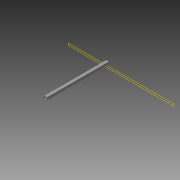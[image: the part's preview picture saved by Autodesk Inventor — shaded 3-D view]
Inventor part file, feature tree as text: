
AUTODESK INVENTOR PART (.ipt)
format: ipt  version: 2015 (Build 190159000, 159)  size: 75,776 bytes
history: native  units: in
note: dims shown in document units (in); Inventor stores cm internally (conversion verified against a paired STEP export)
features: plane x1, extrude x1, sketch x1
ambient origin geometry x8: Origin, YZ Plane, XZ Plane, XY Plane, X Axis, Y Axis, Z Axis, Center Point
bodies: Solid1 (feature_tree)
feature tree (3):
  plane  "Work Plane1"
  extrude  "Extrusion1"  Depth=0.75in
  sketch  "Sketch1"  dims[d0=0.75in d1=0.75in d2=0.125in d3=18.0in d4=0.0in]
